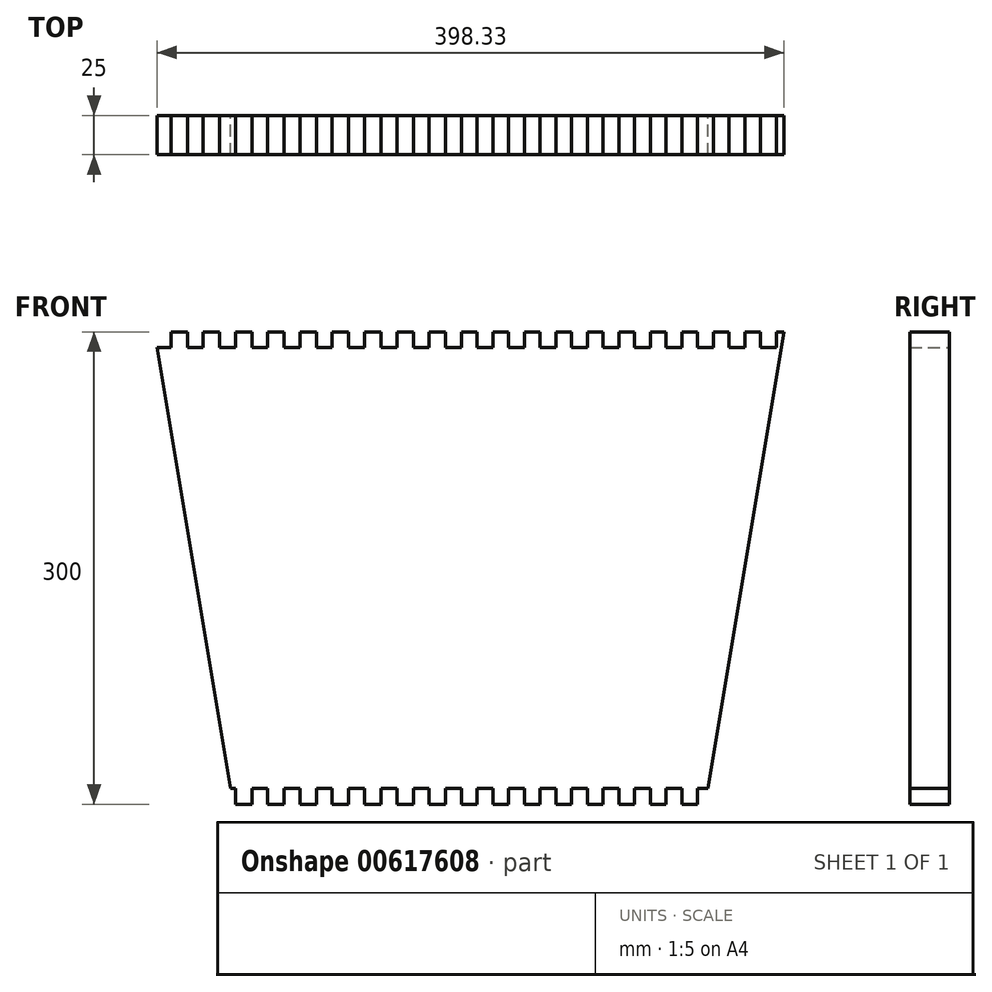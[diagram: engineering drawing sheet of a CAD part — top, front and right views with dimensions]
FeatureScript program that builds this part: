
annotation { "Feature Type Name" : "Feature", "Feature Type Description" : "" }
export const myFeature = defineFeature(function(context is Context, id is Id, definition is map)
    precondition{}
    {
        {
            var Q0;
            Q0=qCreatedBy(makeId("Front.planeOp"),FACE);
            var sketch = newSketch(context, id + "F0", { "sketchPlane" : qUnion([Q0])});
            skLineSegment(sketch, "E0.top", {"start": v(200, 150) * mm, "end": v(-200, 150) * mm});
            skPoint(sketch, "E0.middle", {"position": v(0, 0) * mm});
            skLineSegment(sketch, "E1", {"start": v(-200, 150) * mm, "end": v(-150, -150) * mm});
            skLineSegment(sketch, "E2", {"start": v(150, -150) * mm, "end": v(200, 150) * mm});
            skLineSegment(sketch, "E3.bottom", {"start": v(-5, 150) * mm, "end": v(-15, 150) * mm});
            skLineSegment(sketch, "E3.top", {"start": v(-5, 140) * mm, "end": v(-15, 140) * mm});
            skLineSegment(sketch, "E3.left", {"start": v(-5, 150) * mm, "end": v(-5, 140) * mm});
            skLineSegment(sketch, "E3.right", {"start": v(-15, 150) * mm, "end": v(-15, 140) * mm});
            skLineSegment(sketch, "E4.bottom", {"start": v(5, 150) * mm, "end": v(15, 150) * mm});
            skLineSegment(sketch, "E4.top", {"start": v(5, 140) * mm, "end": v(15, 140) * mm});
            skLineSegment(sketch, "E4.left", {"start": v(5, 150) * mm, "end": v(5, 140) * mm});
            skLineSegment(sketch, "E4.right", {"start": v(15, 150) * mm, "end": v(15, 140) * mm});
            skLineSegment(sketch, "E5.1.0.0", {"start": v(-35.5, 150) * mm, "end": v(-35.5, 140) * mm});
            skLineSegment(sketch, "E5.1.0.1", {"start": v(-25.5, 150) * mm, "end": v(-35.5, 150) * mm});
            skLineSegment(sketch, "E5.1.0.2", {"start": v(-25.5, 140) * mm, "end": v(-35.5, 140) * mm});
            skLineSegment(sketch, "E5.1.0.3", {"start": v(-25.5, 150) * mm, "end": v(-25.5, 140) * mm});
            skLineSegment(sketch, "E5.2.0.0", {"start": v(-56, 150) * mm, "end": v(-56, 140) * mm});
            skLineSegment(sketch, "E5.2.0.1", {"start": v(-46, 150) * mm, "end": v(-56, 150) * mm});
            skLineSegment(sketch, "E5.2.0.2", {"start": v(-46, 140) * mm, "end": v(-56, 140) * mm});
            skLineSegment(sketch, "E5.2.0.3", {"start": v(-46, 150) * mm, "end": v(-46, 140) * mm});
            skLineSegment(sketch, "E5.3.0.0", {"start": v(-76.5, 150) * mm, "end": v(-76.5, 140) * mm});
            skLineSegment(sketch, "E5.3.0.1", {"start": v(-66.5, 150) * mm, "end": v(-76.5, 150) * mm});
            skLineSegment(sketch, "E5.3.0.2", {"start": v(-66.5, 140) * mm, "end": v(-76.5, 140) * mm});
            skLineSegment(sketch, "E5.3.0.3", {"start": v(-66.5, 150) * mm, "end": v(-66.5, 140) * mm});
            skLineSegment(sketch, "E5.4.0.0", {"start": v(-97, 150) * mm, "end": v(-97, 140) * mm});
            skLineSegment(sketch, "E5.4.0.1", {"start": v(-87, 150) * mm, "end": v(-97, 150) * mm});
            skLineSegment(sketch, "E5.4.0.2", {"start": v(-87, 140) * mm, "end": v(-97, 140) * mm});
            skLineSegment(sketch, "E5.4.0.3", {"start": v(-87, 150) * mm, "end": v(-87, 140) * mm});
            skLineSegment(sketch, "E5.5.0.0", {"start": v(-117.5, 150) * mm, "end": v(-117.5, 140) * mm});
            skLineSegment(sketch, "E5.5.0.1", {"start": v(-107.5, 150) * mm, "end": v(-117.5, 150) * mm});
            skLineSegment(sketch, "E5.5.0.2", {"start": v(-107.5, 140) * mm, "end": v(-117.5, 140) * mm});
            skLineSegment(sketch, "E5.5.0.3", {"start": v(-107.5, 150) * mm, "end": v(-107.5, 140) * mm});
            skLineSegment(sketch, "E5.6.0.0", {"start": v(-138, 150) * mm, "end": v(-138, 140) * mm});
            skLineSegment(sketch, "E5.6.0.1", {"start": v(-128, 150) * mm, "end": v(-138, 150) * mm});
            skLineSegment(sketch, "E5.6.0.2", {"start": v(-128, 140) * mm, "end": v(-138, 140) * mm});
            skLineSegment(sketch, "E5.6.0.3", {"start": v(-128, 150) * mm, "end": v(-128, 140) * mm});
            skLineSegment(sketch, "E5.7.0.0", {"start": v(-158.5, 150) * mm, "end": v(-158.5, 140) * mm});
            skLineSegment(sketch, "E5.7.0.1", {"start": v(-148.5, 150) * mm, "end": v(-158.5, 150) * mm});
            skLineSegment(sketch, "E5.7.0.2", {"start": v(-148.5, 140) * mm, "end": v(-158.5, 140) * mm});
            skLineSegment(sketch, "E5.7.0.3", {"start": v(-148.5, 150) * mm, "end": v(-148.5, 140) * mm});
            skLineSegment(sketch, "E5.8.0.0", {"start": v(-179, 150) * mm, "end": v(-179, 140) * mm});
            skLineSegment(sketch, "E5.8.0.1", {"start": v(-169, 150) * mm, "end": v(-179, 150) * mm});
            skLineSegment(sketch, "E5.8.0.2", {"start": v(-169, 140) * mm, "end": v(-179, 140) * mm});
            skLineSegment(sketch, "E5.8.0.3", {"start": v(-169, 150) * mm, "end": v(-169, 140) * mm});
            skLineSegment(sketch, "E5.9.0.0", {"start": v(-199.5, 150) * mm, "end": v(-199.5, 140) * mm});
            skLineSegment(sketch, "E5.9.0.1", {"start": v(-189.5, 150) * mm, "end": v(-199.5, 150) * mm});
            skLineSegment(sketch, "E5.9.0.2", {"start": v(-189.5, 140) * mm, "end": v(-199.5, 140) * mm});
            skLineSegment(sketch, "E5.9.0.3", {"start": v(-189.5, 150) * mm, "end": v(-189.5, 140) * mm});
            skLineSegment(sketch, "E5.10.0.0", {"start": v(-220, 150) * mm, "end": v(-220, 140) * mm});
            skLineSegment(sketch, "E5.10.0.1", {"start": v(-210, 150) * mm, "end": v(-220, 150) * mm});
            skLineSegment(sketch, "E5.10.0.2", {"start": v(-210, 140) * mm, "end": v(-220, 140) * mm});
            skLineSegment(sketch, "E5.10.0.3", {"start": v(-210, 150) * mm, "end": v(-210, 140) * mm});
            skLineSegment(sketch, "E6.1.0.0", {"start": v(25, 150) * mm, "end": v(25, 140) * mm});
            skLineSegment(sketch, "E6.1.0.1", {"start": v(25, 140) * mm, "end": v(35, 140) * mm});
            skLineSegment(sketch, "E6.1.0.2", {"start": v(35, 150) * mm, "end": v(35, 140) * mm});
            skLineSegment(sketch, "E6.1.0.3", {"start": v(25, 150) * mm, "end": v(35, 150) * mm});
            skLineSegment(sketch, "E6.2.0.0", {"start": v(45, 150) * mm, "end": v(45, 140) * mm});
            skLineSegment(sketch, "E6.2.0.1", {"start": v(45, 140) * mm, "end": v(55, 140) * mm});
            skLineSegment(sketch, "E6.2.0.2", {"start": v(55, 150) * mm, "end": v(55, 140) * mm});
            skLineSegment(sketch, "E6.2.0.3", {"start": v(45, 150) * mm, "end": v(55, 150) * mm});
            skLineSegment(sketch, "E6.3.0.0", {"start": v(65, 150) * mm, "end": v(65, 140) * mm});
            skLineSegment(sketch, "E6.3.0.1", {"start": v(65, 140) * mm, "end": v(75, 140) * mm});
            skLineSegment(sketch, "E6.3.0.2", {"start": v(75, 150) * mm, "end": v(75, 140) * mm});
            skLineSegment(sketch, "E6.3.0.3", {"start": v(65, 150) * mm, "end": v(75, 150) * mm});
            skLineSegment(sketch, "E6.4.0.0", {"start": v(85, 150) * mm, "end": v(85, 140) * mm});
            skLineSegment(sketch, "E6.4.0.1", {"start": v(85, 140) * mm, "end": v(95, 140) * mm});
            skLineSegment(sketch, "E6.4.0.2", {"start": v(95, 150) * mm, "end": v(95, 140) * mm});
            skLineSegment(sketch, "E6.4.0.3", {"start": v(85, 150) * mm, "end": v(95, 150) * mm});
            skLineSegment(sketch, "E6.5.0.0", {"start": v(105, 150) * mm, "end": v(105, 140) * mm});
            skLineSegment(sketch, "E6.5.0.1", {"start": v(105, 140) * mm, "end": v(115, 140) * mm});
            skLineSegment(sketch, "E6.5.0.2", {"start": v(115, 150) * mm, "end": v(115, 140) * mm});
            skLineSegment(sketch, "E6.5.0.3", {"start": v(105, 150) * mm, "end": v(115, 150) * mm});
            skLineSegment(sketch, "E6.6.0.0", {"start": v(125, 150) * mm, "end": v(125, 140) * mm});
            skLineSegment(sketch, "E6.6.0.1", {"start": v(125, 140) * mm, "end": v(135, 140) * mm});
            skLineSegment(sketch, "E6.6.0.2", {"start": v(135, 150) * mm, "end": v(135, 140) * mm});
            skLineSegment(sketch, "E6.6.0.3", {"start": v(125, 150) * mm, "end": v(135, 150) * mm});
            skLineSegment(sketch, "E6.7.0.0", {"start": v(145, 150) * mm, "end": v(145, 140) * mm});
            skLineSegment(sketch, "E6.7.0.1", {"start": v(145, 140) * mm, "end": v(155, 140) * mm});
            skLineSegment(sketch, "E6.7.0.2", {"start": v(155, 150) * mm, "end": v(155, 140) * mm});
            skLineSegment(sketch, "E6.7.0.3", {"start": v(145, 150) * mm, "end": v(155, 150) * mm});
            skLineSegment(sketch, "E6.8.0.0", {"start": v(165, 150) * mm, "end": v(165, 140) * mm});
            skLineSegment(sketch, "E6.8.0.1", {"start": v(165, 140) * mm, "end": v(175, 140) * mm});
            skLineSegment(sketch, "E6.8.0.2", {"start": v(175, 150) * mm, "end": v(175, 140) * mm});
            skLineSegment(sketch, "E6.8.0.3", {"start": v(165, 150) * mm, "end": v(175, 150) * mm});
            skLineSegment(sketch, "E6.9.0.0", {"start": v(185, 150) * mm, "end": v(185, 140) * mm});
            skLineSegment(sketch, "E6.9.0.1", {"start": v(185, 140) * mm, "end": v(195, 140) * mm});
            skLineSegment(sketch, "E6.9.0.2", {"start": v(195, 150) * mm, "end": v(195, 140) * mm});
            skLineSegment(sketch, "E6.9.0.3", {"start": v(185, 150) * mm, "end": v(195, 150) * mm});
            skLineSegment(sketch, "E6.10.0.0", {"start": v(205, 150) * mm, "end": v(205, 140) * mm});
            skLineSegment(sketch, "E6.10.0.1", {"start": v(205, 140) * mm, "end": v(215, 140) * mm});
            skLineSegment(sketch, "E6.10.0.2", {"start": v(215, 150) * mm, "end": v(215, 140) * mm});
            skLineSegment(sketch, "E6.10.0.3", {"start": v(205, 150) * mm, "end": v(215, 150) * mm});
            skLineSegment(sketch, "E7", {"start": v(0, 150) * mm, "end": v(-5, 150) * mm});
            skLineSegment(sketch, "E8", {"start": v(5, 150) * mm, "end": v(0, 150) * mm});
            skLineSegment(sketch, "E9", {"start": v(-150, -150) * mm, "end": v(150, -150) * mm});
            skLineSegment(sketch, "E10.MirrorCS", {"start": v(-56, -150) * mm, "end": v(-56, -140) * mm});
            skLineSegment(sketch, "E11.MirrorCS", {"start": v(-138, -150) * mm, "end": v(-138, -140) * mm});
            skLineSegment(sketch, "E12.MirrorCS", {"start": v(-117.5, -150) * mm, "end": v(-117.5, -140) * mm});
            skLineSegment(sketch, "E13.MirrorCS", {"start": v(-87, -150) * mm, "end": v(-87, -140) * mm});
            skLineSegment(sketch, "E14.MirrorCS", {"start": v(-169, -150) * mm, "end": v(-169, -140) * mm});
            skLineSegment(sketch, "E15.MirrorCS", {"start": v(-128, -150) * mm, "end": v(-138, -150) * mm});
            skLineSegment(sketch, "E16.MirrorCS", {"start": v(-46, -150) * mm, "end": v(-56, -150) * mm});
            skLineSegment(sketch, "E17.MirrorCS", {"start": v(-179, -150) * mm, "end": v(-179, -140) * mm});
            skLineSegment(sketch, "E18.MirrorCS", {"start": v(-35.5, -150) * mm, "end": v(-35.5, -140) * mm});
            skLineSegment(sketch, "E19.MirrorCS", {"start": v(-5, -140) * mm, "end": v(-15, -140) * mm});
            skLineSegment(sketch, "E20.MirrorCS", {"start": v(-25.5, -140) * mm, "end": v(-35.5, -140) * mm});
            skLineSegment(sketch, "E21.MirrorCS", {"start": v(-148.5, -150) * mm, "end": v(-148.5, -140) * mm});
            skLineSegment(sketch, "E22.MirrorCS", {"start": v(85, -150) * mm, "end": v(85, -140) * mm});
            skLineSegment(sketch, "E23.MirrorCS", {"start": v(-66.5, -150) * mm, "end": v(-66.5, -140) * mm});
            skLineSegment(sketch, "E24.MirrorCS", {"start": v(-148.5, -140) * mm, "end": v(-158.5, -140) * mm});
            skLineSegment(sketch, "E25.MirrorCS", {"start": v(-107.5, -150) * mm, "end": v(-107.5, -140) * mm});
            skLineSegment(sketch, "E26.MirrorCS", {"start": v(-66.5, -140) * mm, "end": v(-76.5, -140) * mm});
            skLineSegment(sketch, "E27.MirrorCS", {"start": v(-107.5, -150) * mm, "end": v(-117.5, -150) * mm});
            skLineSegment(sketch, "E28.MirrorCS", {"start": v(-107.5, -140) * mm, "end": v(-117.5, -140) * mm});
            skLineSegment(sketch, "E29.MirrorCS", {"start": v(-148.5, -150) * mm, "end": v(-158.5, -150) * mm});
            skLineSegment(sketch, "E30.MirrorCS", {"start": v(75, -150) * mm, "end": v(75, -140) * mm});
            skLineSegment(sketch, "E31.MirrorCS", {"start": v(-66.5, -150) * mm, "end": v(-76.5, -150) * mm});
            skLineSegment(sketch, "E32.MirrorCS", {"start": v(145, -150) * mm, "end": v(145, -140) * mm});
            skLineSegment(sketch, "E33.MirrorCS", {"start": v(0, -150) * mm, "end": v(-5, -150) * mm});
            skLineSegment(sketch, "E34.MirrorCS", {"start": v(-199.5, -150) * mm, "end": v(-199.5, -140) * mm});
            skLineSegment(sketch, "E35.MirrorCS", {"start": v(65, -150) * mm, "end": v(65, -140) * mm});
            skLineSegment(sketch, "E36.MirrorCS", {"start": v(105, -150) * mm, "end": v(105, -140) * mm});
            skLineSegment(sketch, "E37.MirrorCS", {"start": v(-76.5, -150) * mm, "end": v(-76.5, -140) * mm});
            skLineSegment(sketch, "E38.MirrorCS", {"start": v(-128, -150) * mm, "end": v(-128, -140) * mm});
            skLineSegment(sketch, "E39.MirrorCS", {"start": v(-87, -140) * mm, "end": v(-97, -140) * mm});
            skLineSegment(sketch, "E40.MirrorCS", {"start": v(-169, -140) * mm, "end": v(-179, -140) * mm});
            skLineSegment(sketch, "E41.MirrorCS", {"start": v(-128, -140) * mm, "end": v(-138, -140) * mm});
            skLineSegment(sketch, "E42.MirrorCS", {"start": v(-46, -140) * mm, "end": v(-56, -140) * mm});
            skLineSegment(sketch, "E43.MirrorCS", {"start": v(-87, -150) * mm, "end": v(-97, -150) * mm});
            skLineSegment(sketch, "E44.MirrorCS", {"start": v(-169, -150) * mm, "end": v(-179, -150) * mm});
            skLineSegment(sketch, "E45.MirrorCS", {"start": v(-97, -150) * mm, "end": v(-97, -140) * mm});
            skLineSegment(sketch, "E46.MirrorCS", {"start": v(-158.5, -150) * mm, "end": v(-158.5, -140) * mm});
            skLineSegment(sketch, "E47.MirrorCS", {"start": v(-46, -150) * mm, "end": v(-46, -140) * mm});
            skLineSegment(sketch, "E48.MirrorCS", {"start": v(95, -150) * mm, "end": v(95, -140) * mm});
            skLineSegment(sketch, "E49.MirrorCS", {"start": v(125, -140) * mm, "end": v(135, -140) * mm});
            skLineSegment(sketch, "E50.MirrorCS", {"start": v(125, -150) * mm, "end": v(125, -140) * mm});
            skLineSegment(sketch, "E51.MirrorCS", {"start": v(45, -150) * mm, "end": v(45, -140) * mm});
            skLineSegment(sketch, "E52.MirrorCS", {"start": v(15, -150) * mm, "end": v(15, -140) * mm});
            skLineSegment(sketch, "E53.MirrorCS", {"start": v(5, -150) * mm, "end": v(5, -140) * mm});
            skLineSegment(sketch, "E54.MirrorCS", {"start": v(5, -140) * mm, "end": v(15, -140) * mm});
            skLineSegment(sketch, "E55.MirrorCS", {"start": v(5, -150) * mm, "end": v(15, -150) * mm});
            skLineSegment(sketch, "E56.MirrorCS", {"start": v(-15, -150) * mm, "end": v(-15, -140) * mm});
            skLineSegment(sketch, "E57.MirrorCS", {"start": v(-5, -150) * mm, "end": v(-5, -140) * mm});
            skLineSegment(sketch, "E58.MirrorCS", {"start": v(-5, -150) * mm, "end": v(-15, -150) * mm});
            skLineSegment(sketch, "E59.MirrorCS", {"start": v(-25.5, -150) * mm, "end": v(-25.5, -140) * mm});
            skLineSegment(sketch, "E60.MirrorCS", {"start": v(115, -150) * mm, "end": v(115, -140) * mm});
            skLineSegment(sketch, "E61.MirrorCS", {"start": v(65, -150) * mm, "end": v(75, -150) * mm});
            skLineSegment(sketch, "E62.MirrorCS", {"start": v(145, -150) * mm, "end": v(155, -150) * mm});
            skLineSegment(sketch, "E63.MirrorCS", {"start": v(145, -140) * mm, "end": v(155, -140) * mm});
            skLineSegment(sketch, "E64.MirrorCS", {"start": v(5, -150) * mm, "end": v(0, -150) * mm});
            skLineSegment(sketch, "E65.MirrorCS", {"start": v(-189.5, -150) * mm, "end": v(-199.5, -150) * mm});
            skLineSegment(sketch, "E66.MirrorCS", {"start": v(25, -140) * mm, "end": v(35, -140) * mm});
            skLineSegment(sketch, "E67.MirrorCS", {"start": v(105, -140) * mm, "end": v(115, -140) * mm});
            skLineSegment(sketch, "E68.MirrorCS", {"start": v(155, -150) * mm, "end": v(155, -140) * mm});
            skLineSegment(sketch, "E69.MirrorCS", {"start": v(125, -150) * mm, "end": v(135, -150) * mm});
            skLineSegment(sketch, "E70.MirrorCS", {"start": v(135, -150) * mm, "end": v(135, -140) * mm});
            skLineSegment(sketch, "E71.MirrorCS", {"start": v(55, -150) * mm, "end": v(55, -140) * mm});
            skLineSegment(sketch, "E72.MirrorCS", {"start": v(45, -140) * mm, "end": v(55, -140) * mm});
            skLineSegment(sketch, "E73.MirrorCS", {"start": v(85, -140) * mm, "end": v(95, -140) * mm});
            skLineSegment(sketch, "E74.MirrorCS", {"start": v(-25.5, -150) * mm, "end": v(-35.5, -150) * mm});
            skLineSegment(sketch, "E75.MirrorCS", {"start": v(105, -150) * mm, "end": v(115, -150) * mm});
            skLineSegment(sketch, "E76.MirrorCS", {"start": v(-189.5, -150) * mm, "end": v(-189.5, -140) * mm});
            skLineSegment(sketch, "E77.MirrorCS", {"start": v(65, -140) * mm, "end": v(75, -140) * mm});
            skLineSegment(sketch, "E78.MirrorCS", {"start": v(-189.5, -140) * mm, "end": v(-199.5, -140) * mm});
            skLineSegment(sketch, "E79.MirrorCS", {"start": v(85, -150) * mm, "end": v(95, -150) * mm});
            skLineSegment(sketch, "E80.MirrorCS", {"start": v(25, -150) * mm, "end": v(25, -140) * mm});
            skLineSegment(sketch, "E81.MirrorCS", {"start": v(45, -150) * mm, "end": v(55, -150) * mm});
            skLineSegment(sketch, "E82.MirrorCS", {"start": v(165, -140) * mm, "end": v(175, -140) * mm});
            skLineSegment(sketch, "E83.MirrorCS", {"start": v(25, -150) * mm, "end": v(35, -150) * mm});
            skLineSegment(sketch, "E84.MirrorCS", {"start": v(35, -150) * mm, "end": v(35, -140) * mm});
            skLineSegment(sketch, "E85.MirrorCS", {"start": v(185, -150) * mm, "end": v(185, -140) * mm});
            skLineSegment(sketch, "E86.MirrorCS", {"start": v(175, -150) * mm, "end": v(175, -140) * mm});
            skLineSegment(sketch, "E87.MirrorCS", {"start": v(165, -150) * mm, "end": v(165, -140) * mm});
            skLineSegment(sketch, "E88.MirrorCS", {"start": v(165, -150) * mm, "end": v(175, -150) * mm});
            skLineSegment(sketch, "E89.MirrorCS", {"start": v(205, -140) * mm, "end": v(215, -140) * mm});
            skLineSegment(sketch, "E90.MirrorCS", {"start": v(205, -150) * mm, "end": v(205, -140) * mm});
            skLineSegment(sketch, "E91.MirrorCS", {"start": v(200, -150) * mm, "end": v(-200, -150) * mm});
            skLineSegment(sketch, "E92.MirrorCS", {"start": v(185, -150) * mm, "end": v(195, -150) * mm});
            skLineSegment(sketch, "E93.MirrorCS", {"start": v(195, -150) * mm, "end": v(195, -140) * mm});
            skLineSegment(sketch, "E94.MirrorCS", {"start": v(185, -140) * mm, "end": v(195, -140) * mm});
            skLineSegment(sketch, "E95.MirrorCS", {"start": v(-210, -150) * mm, "end": v(-210, -140) * mm});
            skLineSegment(sketch, "E96.MirrorCS", {"start": v(-220, -150) * mm, "end": v(-220, -140) * mm});
            skLineSegment(sketch, "E97.MirrorCS", {"start": v(205, -150) * mm, "end": v(215, -150) * mm});
            skLineSegment(sketch, "E98.MirrorCS", {"start": v(-210, -140) * mm, "end": v(-220, -140) * mm});
            skLineSegment(sketch, "E99.MirrorCS", {"start": v(-210, -150) * mm, "end": v(-220, -150) * mm});
            skLineSegment(sketch, "E100.MirrorCS", {"start": v(215, -150) * mm, "end": v(215, -140) * mm});
            skSolve(sketch);
        }
        {
            var Q0;
            Q0=makeQuery(id+"F0.imprint","IMPRINT",FACE,{"disambiguationData":[TD([[makeQuery(id+"F0.imprint","IMPRINT",EDGE,{"derivedFrom":sQuery(id+"F0.wireOp",EDGE,"E3.top")}),1.0]])]});
            extrude(context, id + "F1", {"entities" : qUnion([Q0]), "depth" : 25 * mm, "offsetDistance" : 25 * mm});
        }
    });
